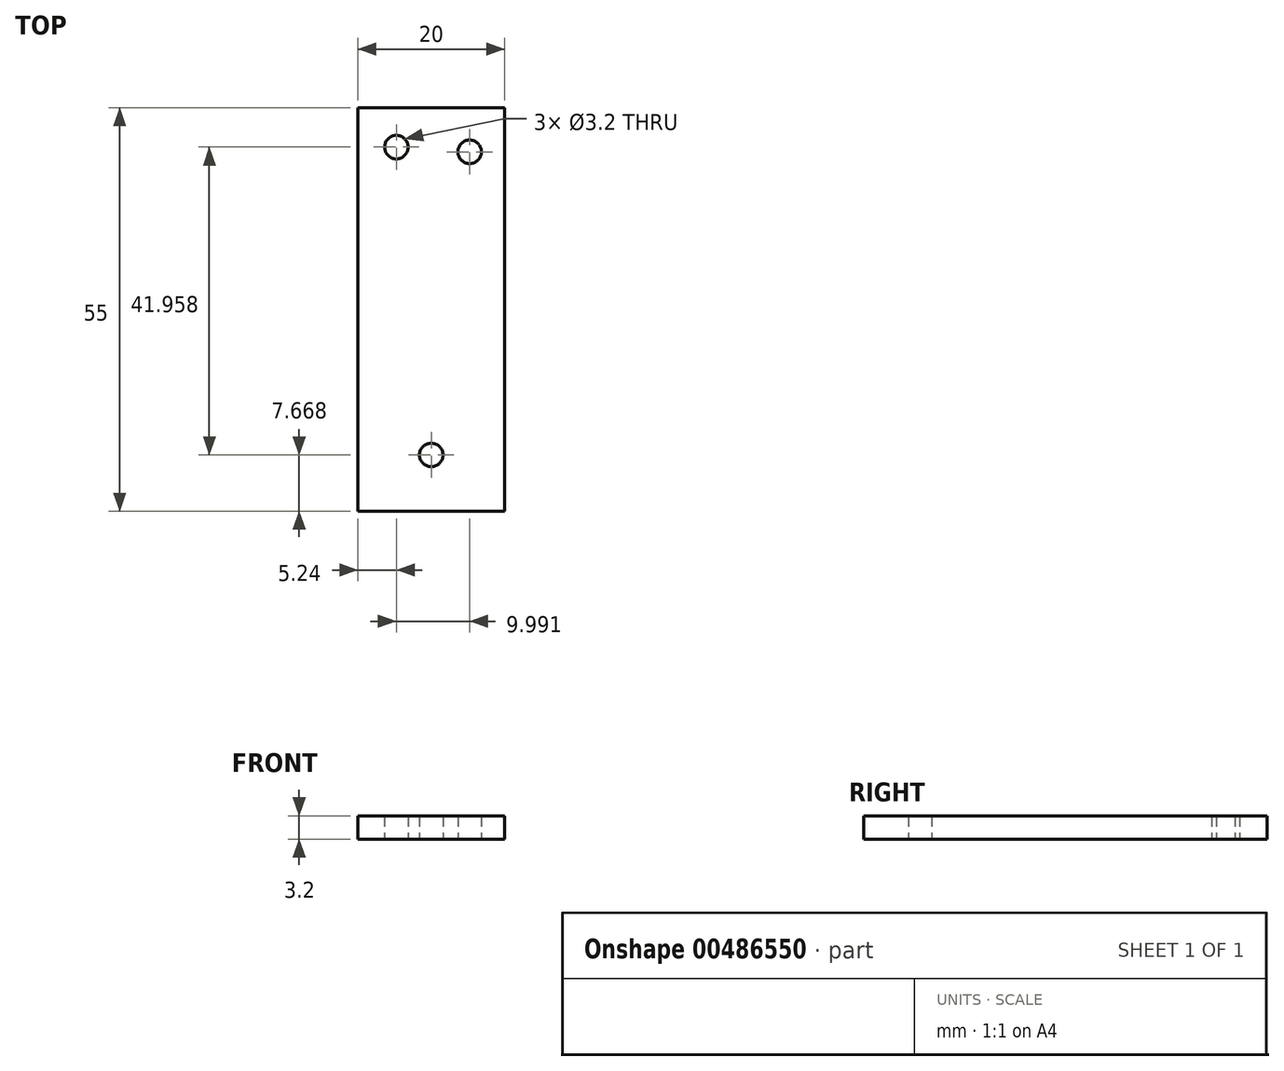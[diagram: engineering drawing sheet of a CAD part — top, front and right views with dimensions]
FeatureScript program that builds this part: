
annotation { "Feature Type Name" : "Feature", "Feature Type Description" : "" }
export const myFeature = defineFeature(function(context is Context, id is Id, definition is map)
    precondition{}
    {
        {
            var Q0;
            Q0=qCreatedBy(makeId("Top.planeOp"),FACE);
            var sketch = newSketch(context, id + "F0", { "sketchPlane" : qUnion([Q0])});
            skLineSegment(sketch, "E0.bottom", {"start": v(-10, -27.5) * mm, "end": v(10, -27.5) * mm});
            skLineSegment(sketch, "E0.top", {"start": v(-10, 27.5) * mm, "end": v(10, 27.5) * mm});
            skLineSegment(sketch, "E0.left", {"start": v(-10, -27.5) * mm, "end": v(-10, 27.5) * mm});
            skLineSegment(sketch, "E0.right", {"start": v(10, -27.5) * mm, "end": v(10, 27.5) * mm});
            skPoint(sketch, "E0.middle", {"position": v(0, 0) * mm});
            skCircle(sketch, "E1", {"center": v(0, -19.83) * mm, "radius": 1.6 * mm});
            skCircle(sketch, "E2", {"center": v(5.23, 21.49) * mm, "radius": 1.6 * mm});
            skCircle(sketch, "E3", {"center": v(-4.76, 22.13) * mm, "radius": 1.6 * mm});
            skSolve(sketch);
        }
        {
            var Q0;
            Q0=makeQuery(id+"F0.imprint","IMPRINT",FACE,{"disambiguationData":[TD([[makeQuery(id+"F0.imprint","IMPRINT",EDGE,{"derivedFrom":sQuery(id+"F0.wireOp",EDGE,"E0.bottom")}),1.0]])]});
            extrude(context, id + "F1", {"entities" : qUnion([Q0]), "depth" : 3.2 * mm, "offsetDistance" : 25 * mm});
        }
        {
            var Q0;
            Q0=makeQuery(id+"F0.imprint","IMPRINT",FACE,{"disambiguationData":[TD([[makeQuery(id+"F0.imprint","IMPRINT",EDGE,{"derivedFrom":sQuery(id+"F0.wireOp",EDGE,"E0.bottom")}),1.0]])]});
            extrude(context, id + "F2", {"entities" : qUnion([Q0]), "operationType" : NewBodyOperationType.ADD, "depth" : 3.2 * mm, "offsetDistance" : 25 * mm});
        }
        {
            var Q0;
            Q0=makeQuery(id+"F0.imprint","IMPRINT",FACE,{"disambiguationData":[TD([[makeQuery(id+"F0.imprint","IMPRINT",EDGE,{"derivedFrom":sQuery(id+"F0.wireOp",EDGE,"E0.bottom")}),1.0]])]});
            extrude(context, id + "F3", {"entities" : qUnion([Q0]), "operationType" : NewBodyOperationType.ADD, "depth" : 3.2 * mm, "offsetDistance" : 25 * mm});
        }
    });
